annotation { "Feature Type Name" : "Feature", "Feature Type Description" : "" }
export const myFeature = defineFeature(function(context is Context, id is Id, definition is map)
    precondition{}
    {
        {
            var Q0;
            Q0=qCreatedBy(makeId("Top.planeOp"),FACE);
            var sketch = newSketch(context, id + "F0", { "sketchPlane" : qUnion([Q0])});
            skLineSegment(sketch, "E0.bottom", {"start": v(-152.53, 68.83) * mm, "end": v(-142.37, 68.83) * mm});
            skLineSegment(sketch, "E0.top", {"start": v(-142.37, 14.85) * mm, "end": v(-132.2, 14.85) * mm});
            skLineSegment(sketch, "E0.left", {"start": v(-152.53, 68.83) * mm, "end": v(-152.53, 58.67) * mm});
            skLineSegment(sketch, "E0.right", {"start": v(-98.55, 58.67) * mm, "end": v(-98.55, 48.5) * mm});
            skLineSegment(sketch, "E1", {"start": v(-132.2, 68.83) * mm, "end": v(-132.2, 65.65) * mm});
            skLineSegment(sketch, "E2", {"start": v(-132.2, 65.65) * mm, "end": v(-142.37, 65.65) * mm});
            skLineSegment(sketch, "E3", {"start": v(-142.37, 65.65) * mm, "end": v(-142.37, 68.83) * mm});
            skLineSegment(sketch, "E4.top", {"start": v(-122.05, 65.65) * mm, "end": v(-111.89, 65.65) * mm});
            skLineSegment(sketch, "E4.left", {"start": v(-122.05, 68.83) * mm, "end": v(-122.05, 65.65) * mm});
            skLineSegment(sketch, "E4.right", {"start": v(-111.89, 68.83) * mm, "end": v(-111.89, 65.65) * mm});
            skLineSegment(sketch, "E5.top", {"start": v(-101.73, 58.67) * mm, "end": v(-98.55, 58.67) * mm});
            skLineSegment(sketch, "E5.left", {"start": v(-101.73, 68.83) * mm, "end": v(-101.73, 58.67) * mm});
            skLineSegment(sketch, "E6.bottom", {"start": v(-101.73, 48.5) * mm, "end": v(-98.55, 48.5) * mm});
            skLineSegment(sketch, "E6.top", {"start": v(-101.73, 38.35) * mm, "end": v(-98.55, 38.35) * mm});
            skLineSegment(sketch, "E6.left", {"start": v(-101.73, 48.5) * mm, "end": v(-101.73, 38.35) * mm});
            skLineSegment(sketch, "E7.bottom", {"start": v(-101.73, 28.19) * mm, "end": v(-98.55, 28.19) * mm});
            skLineSegment(sketch, "E7.left", {"start": v(-101.73, 28.19) * mm, "end": v(-101.73, 18.03) * mm});
            skLineSegment(sketch, "E8.bottom", {"start": v(-101.73, 18.03) * mm, "end": v(-111.89, 18.03) * mm});
            skLineSegment(sketch, "E8.right", {"start": v(-111.89, 18.03) * mm, "end": v(-111.89, 14.85) * mm});
            skLineSegment(sketch, "E9.top", {"start": v(-122.05, 18.03) * mm, "end": v(-132.2, 18.03) * mm});
            skLineSegment(sketch, "E9.left", {"start": v(-122.05, 14.85) * mm, "end": v(-122.05, 18.03) * mm});
            skLineSegment(sketch, "E9.right", {"start": v(-132.2, 14.85) * mm, "end": v(-132.2, 18.03) * mm});
            skLineSegment(sketch, "E10.top", {"start": v(-142.37, 18.03) * mm, "end": v(-152.53, 18.03) * mm});
            skLineSegment(sketch, "E10.left", {"start": v(-142.37, 14.85) * mm, "end": v(-142.37, 18.03) * mm});
            skLineSegment(sketch, "E11.bottom", {"start": v(-152.53, 58.67) * mm, "end": v(-149.35, 58.67) * mm});
            skLineSegment(sketch, "E11.top", {"start": v(-152.53, 48.5) * mm, "end": v(-149.35, 48.5) * mm});
            skLineSegment(sketch, "E11.right", {"start": v(-149.35, 58.67) * mm, "end": v(-149.35, 48.5) * mm});
            skLineSegment(sketch, "E12.bottom", {"start": v(-152.53, 38.35) * mm, "end": v(-149.35, 38.35) * mm});
            skLineSegment(sketch, "E12.top", {"start": v(-152.53, 28.19) * mm, "end": v(-149.35, 28.19) * mm});
            skLineSegment(sketch, "E12.right", {"start": v(-149.35, 38.35) * mm, "end": v(-149.35, 28.19) * mm});
            skLineSegment(sketch, "E13.trimOffspring", {"start": v(-152.53, 48.5) * mm, "end": v(-152.53, 38.35) * mm});
            skLineSegment(sketch, "E14.trimOffspring", {"start": v(-152.53, 28.19) * mm, "end": v(-152.53, 18.03) * mm});
            skPoint(sketch, "E15.top.end.orphan", {"position": v(0, 0) * mm});
            skLineSegment(sketch, "E16.trimOffspring", {"start": v(-132.2, 68.83) * mm, "end": v(-122.05, 68.83) * mm});
            skLineSegment(sketch, "E17.trimOffspring", {"start": v(-111.89, 68.83) * mm, "end": v(-101.73, 68.83) * mm});
            skLineSegment(sketch, "E18.trimOffspring", {"start": v(-98.55, 38.35) * mm, "end": v(-98.55, 28.19) * mm});
            skLineSegment(sketch, "E19.trimOffspring", {"start": v(-122.05, 14.85) * mm, "end": v(-111.89, 14.85) * mm});
            skLineSegment(sketch, "E20.bottom", {"start": v(-101.73, 68.83) * mm, "end": v(-91.57, 68.83) * mm});
            skLineSegment(sketch, "E20.top", {"start": v(-91.57, 14.85) * mm, "end": v(-81.4, 14.85) * mm});
            skLineSegment(sketch, "E20.right", {"start": v(-47.75, 58.67) * mm, "end": v(-47.75, 48.5) * mm});
            skLineSegment(sketch, "E21", {"start": v(-81.4, 68.83) * mm, "end": v(-81.4, 65.65) * mm});
            skLineSegment(sketch, "E22", {"start": v(-81.4, 65.65) * mm, "end": v(-91.57, 65.65) * mm});
            skLineSegment(sketch, "E23", {"start": v(-91.57, 65.65) * mm, "end": v(-91.57, 68.83) * mm});
            skLineSegment(sketch, "E24.top", {"start": v(-71.25, 65.65) * mm, "end": v(-61.09, 65.65) * mm});
            skLineSegment(sketch, "E24.left", {"start": v(-71.25, 68.83) * mm, "end": v(-71.25, 65.65) * mm});
            skLineSegment(sketch, "E24.right", {"start": v(-61.09, 68.83) * mm, "end": v(-61.09, 65.65) * mm});
            skLineSegment(sketch, "E25.top", {"start": v(-50.93, 58.67) * mm, "end": v(-47.75, 58.67) * mm});
            skLineSegment(sketch, "E25.left", {"start": v(-50.93, 68.83) * mm, "end": v(-50.93, 58.67) * mm});
            skLineSegment(sketch, "E26.bottom", {"start": v(-50.93, 48.5) * mm, "end": v(-47.75, 48.5) * mm});
            skLineSegment(sketch, "E26.top", {"start": v(-50.93, 38.35) * mm, "end": v(-47.75, 38.35) * mm});
            skLineSegment(sketch, "E26.left", {"start": v(-50.93, 48.5) * mm, "end": v(-50.93, 38.35) * mm});
            skLineSegment(sketch, "E27.bottom", {"start": v(-50.93, 28.19) * mm, "end": v(-47.75, 28.19) * mm});
            skLineSegment(sketch, "E27.left", {"start": v(-50.93, 28.19) * mm, "end": v(-50.93, 18.03) * mm});
            skLineSegment(sketch, "E28.bottom", {"start": v(-50.93, 18.03) * mm, "end": v(-61.09, 18.03) * mm});
            skLineSegment(sketch, "E28.right", {"start": v(-61.09, 18.03) * mm, "end": v(-61.09, 14.85) * mm});
            skLineSegment(sketch, "E29.top", {"start": v(-71.25, 18.03) * mm, "end": v(-81.4, 18.03) * mm});
            skLineSegment(sketch, "E29.left", {"start": v(-71.25, 14.85) * mm, "end": v(-71.25, 18.03) * mm});
            skLineSegment(sketch, "E29.right", {"start": v(-81.4, 14.85) * mm, "end": v(-81.4, 18.03) * mm});
            skLineSegment(sketch, "E30.top", {"start": v(-91.57, 18.03) * mm, "end": v(-101.73, 18.03) * mm});
            skLineSegment(sketch, "E30.left", {"start": v(-91.57, 14.85) * mm, "end": v(-91.57, 18.03) * mm});
            skPoint(sketch, "E31.top.end.orphan", {"position": v(51, 1.86) * mm});
            skLineSegment(sketch, "E32.trimOffspring", {"start": v(-81.4, 68.83) * mm, "end": v(-71.25, 68.83) * mm});
            skLineSegment(sketch, "E33.trimOffspring", {"start": v(-61.09, 68.83) * mm, "end": v(-50.93, 68.83) * mm});
            skLineSegment(sketch, "E34.trimOffspring", {"start": v(-47.75, 38.35) * mm, "end": v(-47.75, 28.19) * mm});
            skLineSegment(sketch, "E35.trimOffspring", {"start": v(-71.25, 14.85) * mm, "end": v(-61.09, 14.85) * mm});
            skLineSegment(sketch, "E36.bottom", {"start": v(-152.53, 18.03) * mm, "end": v(-142.37, 18.03) * mm});
            skLineSegment(sketch, "E36.left", {"start": v(-152.53, 18.03) * mm, "end": v(-152.53, 7.87) * mm});
            skLineSegment(sketch, "E37", {"start": v(-132.2, 18.03) * mm, "end": v(-132.2, 14.85) * mm});
            skLineSegment(sketch, "E38", {"start": v(-132.2, 14.85) * mm, "end": v(-142.37, 14.85) * mm});
            skLineSegment(sketch, "E39.left", {"start": v(-122.05, 18.03) * mm, "end": v(-122.05, 14.85) * mm});
            skLineSegment(sketch, "E40.bottom", {"start": v(-101.73, -32.77) * mm, "end": v(-111.89, -32.77) * mm});
            skLineSegment(sketch, "E41.top", {"start": v(-122.05, -32.77) * mm, "end": v(-132.2, -32.77) * mm});
            skLineSegment(sketch, "E42.top", {"start": v(-142.37, -32.77) * mm, "end": v(-152.53, -32.77) * mm});
            skLineSegment(sketch, "E43.bottom", {"start": v(-152.53, 7.87) * mm, "end": v(-149.35, 7.87) * mm});
            skLineSegment(sketch, "E43.top", {"start": v(-152.53, -2.3) * mm, "end": v(-149.35, -2.3) * mm});
            skLineSegment(sketch, "E43.right", {"start": v(-149.35, 7.87) * mm, "end": v(-149.35, -2.3) * mm});
            skLineSegment(sketch, "E44.bottom", {"start": v(-152.53, -12.45) * mm, "end": v(-149.35, -12.45) * mm});
            skLineSegment(sketch, "E44.top", {"start": v(-152.53, -22.61) * mm, "end": v(-149.35, -22.61) * mm});
            skLineSegment(sketch, "E44.right", {"start": v(-149.35, -12.45) * mm, "end": v(-149.35, -22.61) * mm});
            skLineSegment(sketch, "E45.trimOffspring", {"start": v(-152.53, -2.3) * mm, "end": v(-152.53, -12.45) * mm});
            skLineSegment(sketch, "E46.trimOffspring", {"start": v(-152.53, -22.61) * mm, "end": v(-152.53, -32.77) * mm});
            skLineSegment(sketch, "E47.trimOffspring", {"start": v(-132.2, 18.03) * mm, "end": v(-122.05, 18.03) * mm});
            skLineSegment(sketch, "E48.trimOffspring", {"start": v(-111.89, 18.03) * mm, "end": v(-101.73, 18.03) * mm});
            skLineSegment(sketch, "E49.bottom", {"start": v(-101.73, 18.03) * mm, "end": v(-95.62, 18.03) * mm});
            skLineSegment(sketch, "E50", {"start": v(-85.39, 14.85) * mm, "end": v(-91.57, 14.85) * mm});
            skLineSegment(sketch, "E51.top", {"start": v(-71.25, 14.85) * mm, "end": v(-65.07, 14.85) * mm});
            skPoint(sketch, "E52.top.end.orphan", {"position": v(0.08, -34.9) * mm});
            skLineSegment(sketch, "E53.trimOffspring", {"start": v(-81.4, 18.03) * mm, "end": v(-75.3, 18.03) * mm});
            skLineSegment(sketch, "E54.trimOffspring", {"start": v(-61.09, 18.03) * mm, "end": v(-54.98, 18.03) * mm});
            skLineSegment(sketch, "E55", {"start": v(-101.73, 18.03) * mm, "end": v(-101.73, 7.87) * mm});
            skLineSegment(sketch, "E56", {"start": v(-101.73, 7.87) * mm, "end": v(-104.9, 7.87) * mm});
            skLineSegment(sketch, "E57", {"start": v(-104.9, 7.87) * mm, "end": v(-104.9, -2.3) * mm});
            skLineSegment(sketch, "E58", {"start": v(-104.9, -2.3) * mm, "end": v(-101.73, -2.3) * mm});
            skLineSegment(sketch, "E59", {"start": v(-101.73, -2.3) * mm, "end": v(-101.73, -12.45) * mm});
            skLineSegment(sketch, "E60", {"start": v(-101.73, -12.45) * mm, "end": v(-104.9, -12.45) * mm});
            skLineSegment(sketch, "E61", {"start": v(-104.9, -12.45) * mm, "end": v(-104.9, -22.61) * mm});
            skLineSegment(sketch, "E62", {"start": v(-104.9, -22.61) * mm, "end": v(-101.73, -22.61) * mm});
            skLineSegment(sketch, "E63", {"start": v(-101.73, -22.61) * mm, "end": v(-101.73, -32.77) * mm});
            skLineSegment(sketch, "E64.left", {"start": v(-200.15, 58.67) * mm, "end": v(-200.15, 48.5) * mm});
            skLineSegment(sketch, "E65.left", {"start": v(-203.33, 68.83) * mm, "end": v(-203.33, 58.67) * mm});
            skLineSegment(sketch, "E66.bottom", {"start": v(-203.33, 48.5) * mm, "end": v(-200.15, 48.5) * mm});
            skLineSegment(sketch, "E66.top", {"start": v(-203.33, 38.35) * mm, "end": v(-200.15, 38.35) * mm});
            skLineSegment(sketch, "E67.bottom", {"start": v(-203.33, 28.19) * mm, "end": v(-200.15, 28.19) * mm});
            skLineSegment(sketch, "E67.left", {"start": v(-203.33, 28.19) * mm, "end": v(-203.33, 18.03) * mm});
            skLineSegment(sketch, "E68.bottom", {"start": v(-203.33, 68.83) * mm, "end": v(-193.17, 68.83) * mm});
            skLineSegment(sketch, "E68.top", {"start": v(-193.17, 14.85) * mm, "end": v(-183, 14.85) * mm});
            skLineSegment(sketch, "E69", {"start": v(-183, 68.83) * mm, "end": v(-183, 65.65) * mm});
            skLineSegment(sketch, "E70", {"start": v(-183, 65.65) * mm, "end": v(-193.17, 65.65) * mm});
            skLineSegment(sketch, "E71", {"start": v(-193.17, 65.65) * mm, "end": v(-193.17, 68.83) * mm});
            skLineSegment(sketch, "E72.top", {"start": v(-172.85, 65.65) * mm, "end": v(-162.69, 65.65) * mm});
            skLineSegment(sketch, "E72.left", {"start": v(-172.85, 68.83) * mm, "end": v(-172.85, 65.65) * mm});
            skLineSegment(sketch, "E72.right", {"start": v(-162.69, 68.83) * mm, "end": v(-162.69, 65.65) * mm});
            skLineSegment(sketch, "E73.bottom", {"start": v(-152.53, 18.03) * mm, "end": v(-162.69, 18.03) * mm});
            skLineSegment(sketch, "E74.top", {"start": v(-172.85, 18.03) * mm, "end": v(-183, 18.03) * mm});
            skLineSegment(sketch, "E75.top", {"start": v(-193.17, 18.03) * mm, "end": v(-203.33, 18.03) * mm});
            skLineSegment(sketch, "E76.bottom", {"start": v(-203.33, 58.67) * mm, "end": v(-200.15, 58.67) * mm});
            skLineSegment(sketch, "E77.right", {"start": v(-200.15, 38.35) * mm, "end": v(-200.15, 28.19) * mm});
            skLineSegment(sketch, "E78.trimOffspring", {"start": v(-203.33, 48.5) * mm, "end": v(-203.33, 38.35) * mm});
            skLineSegment(sketch, "E79.trimOffspring", {"start": v(-183, 68.83) * mm, "end": v(-172.85, 68.83) * mm});
            skLineSegment(sketch, "E80.trimOffspring", {"start": v(-162.69, 68.83) * mm, "end": v(-152.53, 68.83) * mm});
            skLineSegment(sketch, "E81.trimOffspring", {"start": v(-172.85, 14.85) * mm, "end": v(-162.69, 14.85) * mm});
            skLineSegment(sketch, "E82", {"start": v(-183, 18.03) * mm, "end": v(-183, 14.85) * mm});
            skLineSegment(sketch, "E83", {"start": v(-183, 14.85) * mm, "end": v(-193.17, 14.85) * mm});
            skLineSegment(sketch, "E84", {"start": v(-193.17, 14.85) * mm, "end": v(-193.17, 18.03) * mm});
            skLineSegment(sketch, "E85.left", {"start": v(-172.85, 18.03) * mm, "end": v(-172.85, 14.85) * mm});
            skLineSegment(sketch, "E85.right", {"start": v(-162.69, 18.03) * mm, "end": v(-162.69, 13.6) * mm});
            skLineSegment(sketch, "E86.bottom", {"start": v(-50.93, 68.83) * mm, "end": v(-40.77, 68.83) * mm});
            skLineSegment(sketch, "E87.left", {"start": v(3.05, 58.67) * mm, "end": v(3.05, 48.5) * mm});
            skLineSegment(sketch, "E88", {"start": v(-30.6, 68.83) * mm, "end": v(-30.6, 65.65) * mm});
            skLineSegment(sketch, "E89", {"start": v(-30.6, 65.65) * mm, "end": v(-40.77, 65.65) * mm});
            skLineSegment(sketch, "E90", {"start": v(-40.77, 65.65) * mm, "end": v(-40.77, 68.83) * mm});
            skLineSegment(sketch, "E91.top", {"start": v(-20.45, 65.65) * mm, "end": v(-10.29, 65.65) * mm});
            skLineSegment(sketch, "E91.left", {"start": v(-20.45, 68.83) * mm, "end": v(-20.45, 65.65) * mm});
            skLineSegment(sketch, "E91.right", {"start": v(-10.29, 68.83) * mm, "end": v(-10.29, 65.65) * mm});
            skLineSegment(sketch, "E92.top", {"start": v(-0.13, 58.67) * mm, "end": v(3.05, 58.67) * mm});
            skLineSegment(sketch, "E92.left", {"start": v(-0.13, 68.83) * mm, "end": v(-0.13, 58.67) * mm});
            skLineSegment(sketch, "E93.bottom", {"start": v(-0.13, 48.5) * mm, "end": v(3.05, 48.5) * mm});
            skLineSegment(sketch, "E93.top", {"start": v(-0.13, 38.35) * mm, "end": v(3.05, 38.35) * mm});
            skLineSegment(sketch, "E93.left", {"start": v(-0.13, 48.5) * mm, "end": v(-0.13, 38.35) * mm});
            skLineSegment(sketch, "E94.bottom", {"start": v(-0.13, 28.19) * mm, "end": v(3.05, 28.19) * mm});
            skLineSegment(sketch, "E94.left", {"start": v(-0.13, 28.19) * mm, "end": v(-0.13, 18.03) * mm});
            skLineSegment(sketch, "E95.bottom", {"start": v(-0.13, 18.03) * mm, "end": v(-10.29, 18.03) * mm});
            skLineSegment(sketch, "E95.right", {"start": v(-10.29, 18.03) * mm, "end": v(-10.29, 14.85) * mm});
            skLineSegment(sketch, "E96.trimOffspring", {"start": v(-30.6, 68.83) * mm, "end": v(-20.45, 68.83) * mm});
            skLineSegment(sketch, "E97.trimOffspring", {"start": v(-10.29, 68.83) * mm, "end": v(-0.13, 68.83) * mm});
            skLineSegment(sketch, "E98.trimOffspring", {"start": v(3.05, 38.35) * mm, "end": v(3.05, 28.19) * mm});
            skLineSegment(sketch, "E99", {"start": v(-10.29, 14.85) * mm, "end": v(-20.45, 14.85) * mm});
            skLineSegment(sketch, "E100", {"start": v(-20.45, 14.85) * mm, "end": v(-20.45, 18.03) * mm});
            skLineSegment(sketch, "E101", {"start": v(-20.45, 18.03) * mm, "end": v(-30.6, 18.03) * mm});
            skLineSegment(sketch, "E102", {"start": v(-30.6, 18.03) * mm, "end": v(-30.6, 14.85) * mm});
            skLineSegment(sketch, "E103", {"start": v(-30.6, 14.85) * mm, "end": v(-40.77, 14.85) * mm});
            skLineSegment(sketch, "E104", {"start": v(-40.77, 14.85) * mm, "end": v(-40.77, 18.03) * mm});
            skLineSegment(sketch, "E105", {"start": v(-40.77, 18.03) * mm, "end": v(-50.93, 18.03) * mm});
            skLineSegment(sketch, "E106", {"start": v(-142.37, -32.77) * mm, "end": v(-142.37, -29.6) * mm});
            skLineSegment(sketch, "E107", {"start": v(-142.37, -29.6) * mm, "end": v(-132.2, -29.6) * mm});
            skLineSegment(sketch, "E108", {"start": v(-132.2, -29.6) * mm, "end": v(-132.2, -32.77) * mm});
            skLineSegment(sketch, "E109", {"start": v(-122.05, -32.77) * mm, "end": v(-122.05, -29.6) * mm});
            skLineSegment(sketch, "E110", {"start": v(-122.05, -29.6) * mm, "end": v(-111.89, -29.6) * mm});
            skLineSegment(sketch, "E111", {"start": v(-111.89, -29.6) * mm, "end": v(-111.89, -32.77) * mm});
            skPoint(sketch, "E51.left.end.orphan", {"position": v(-75.23, 14.85) * mm});
            skPoint(sketch, "E112.top.start.orphan", {"position": v(-148.55, 58.67) * mm});
            skPoint(sketch, "E113.left.start.orphan", {"position": v(-148.55, 48.5) * mm});
            skPoint(sketch, "E113.top.start.orphan", {"position": v(-148.55, 38.35) * mm});
            skPoint(sketch, "E114.left.start.orphan", {"position": v(-148.55, 28.19) * mm});
            skPoint(sketch, "E115.orphan", {"position": v(-146.29, 18.03) * mm});
            skLineSegment(sketch, "E116", {"start": v(-152.53, 68.83) * mm, "end": v(-152.53, 78.99) * mm});
            skLineSegment(sketch, "E117", {"start": v(-152.53, 78.99) * mm, "end": v(-155.7, 78.99) * mm});
            skLineSegment(sketch, "E118", {"start": v(-155.7, 78.99) * mm, "end": v(-155.7, 89.15) * mm});
            skLineSegment(sketch, "E119", {"start": v(-155.7, 89.15) * mm, "end": v(-152.53, 89.15) * mm});
            skLineSegment(sketch, "E120", {"start": v(-152.53, 89.15) * mm, "end": v(-152.53, 99.3) * mm});
            skLineSegment(sketch, "E121", {"start": v(-152.53, 99.3) * mm, "end": v(-155.7, 99.3) * mm});
            skLineSegment(sketch, "E122", {"start": v(-155.7, 99.3) * mm, "end": v(-155.7, 109.47) * mm});
            skLineSegment(sketch, "E123", {"start": v(-155.7, 109.47) * mm, "end": v(-152.53, 109.47) * mm});
            skLineSegment(sketch, "E124", {"start": v(-152.53, 109.47) * mm, "end": v(-152.53, 119.63) * mm});
            skLineSegment(sketch, "E125", {"start": v(-152.53, 119.63) * mm, "end": v(-142.37, 119.63) * mm});
            skLineSegment(sketch, "E126", {"start": v(-142.37, 119.63) * mm, "end": v(-142.37, 122.8) * mm});
            skLineSegment(sketch, "E127", {"start": v(-142.37, 122.8) * mm, "end": v(-132.2, 122.8) * mm});
            skLineSegment(sketch, "E128", {"start": v(-132.2, 122.8) * mm, "end": v(-132.2, 119.63) * mm});
            skLineSegment(sketch, "E129", {"start": v(-132.2, 119.63) * mm, "end": v(-122.05, 119.63) * mm});
            skLineSegment(sketch, "E130", {"start": v(-122.05, 119.63) * mm, "end": v(-122.05, 122.8) * mm});
            skLineSegment(sketch, "E131", {"start": v(-122.05, 122.8) * mm, "end": v(-111.89, 122.8) * mm});
            skLineSegment(sketch, "E132", {"start": v(-111.89, 122.8) * mm, "end": v(-111.89, 119.63) * mm});
            skLineSegment(sketch, "E133", {"start": v(-111.89, 119.63) * mm, "end": v(-101.73, 119.63) * mm});
            skLineSegment(sketch, "E134", {"start": v(-101.73, 119.63) * mm, "end": v(-101.73, 109.47) * mm});
            skLineSegment(sketch, "E135", {"start": v(-101.73, 109.47) * mm, "end": v(-98.55, 109.47) * mm});
            skLineSegment(sketch, "E136", {"start": v(-98.55, 109.47) * mm, "end": v(-98.55, 99.3) * mm});
            skLineSegment(sketch, "E137", {"start": v(-98.55, 99.3) * mm, "end": v(-101.73, 99.3) * mm});
            skLineSegment(sketch, "E138", {"start": v(-101.73, 99.3) * mm, "end": v(-101.73, 89.15) * mm});
            skLineSegment(sketch, "E139", {"start": v(-101.73, 89.15) * mm, "end": v(-98.55, 89.15) * mm});
            skLineSegment(sketch, "E140", {"start": v(-98.55, 89.15) * mm, "end": v(-98.55, 78.99) * mm});
            skLineSegment(sketch, "E141", {"start": v(-98.55, 78.99) * mm, "end": v(-101.73, 78.99) * mm});
            skLineSegment(sketch, "E142", {"start": v(-101.73, 78.99) * mm, "end": v(-101.73, 68.83) * mm});
            skText(sketch, "E143", { "text": "Mia Lei", "fontName": "OpenSans-Regular.ttf"});
            skPoint(sketch, "E144", {"position": v(-152.53, 43.43) * mm});
            skPoint(sketch, "E145", {"position": v(-127.13, 68.83) * mm});
            skPoint(sketch, "E146", {"position": v(-138.74, 43.43) * mm});
            skLineSegment(sketch, "E147", {"start": v(-302.59, 24.55) * mm, "end": v(-302.59, -23.04) * mm});
            skLineSegment(sketch, "E148", {"start": v(-302.59, -23.04) * mm, "end": v(-265.77, -24.84) * mm});
            skLineSegment(sketch, "E149", {"start": v(-265.77, -24.84) * mm, "end": v(-265.77, 22.76) * mm});
            skLineSegment(sketch, "E150", {"start": v(-265.77, 22.76) * mm, "end": v(-302.59, 24.55) * mm});
            const initialGuessF0  = {"E143": [-0.13874, 0.04089, 1, 0, 0.00508]};
            skSetInitialGuess(sketch, initialGuessF0);
            skSolve(sketch);
        }
        {
            var Q0;
            Q0=makeQuery(id+"F0.imprint","IMPRINT",FACE,{"disambiguationData":[TD([[makeQuery(id+"F0.imprint","IMPRINT",EDGE,{"derivedFrom":sQuery(id+"F0.wireOp",EDGE,"E0.left")}),-1.0]])]});
            extrude(context, id + "F1", {"entities" : qUnion([Q0]), "depth" : 3 * mm, "offsetDistance" : 25.4 * mm});
        }
        {
            var Q0;
            Q0=makeQuery(id+"F0.imprint","IMPRINT",FACE,{"disambiguationData":[TD([[makeQuery(id+"F0.imprint","IMPRINT",EDGE,{"derivedFrom":sQuery(id+"F0.wireOp",EDGE,"E0.bottom")}),1.0]])]});
            extrude(context, id + "F2", {"entities" : qUnion([Q0]), "depth" : 3 * mm, "offsetDistance" : 25.4 * mm});
        }
    });